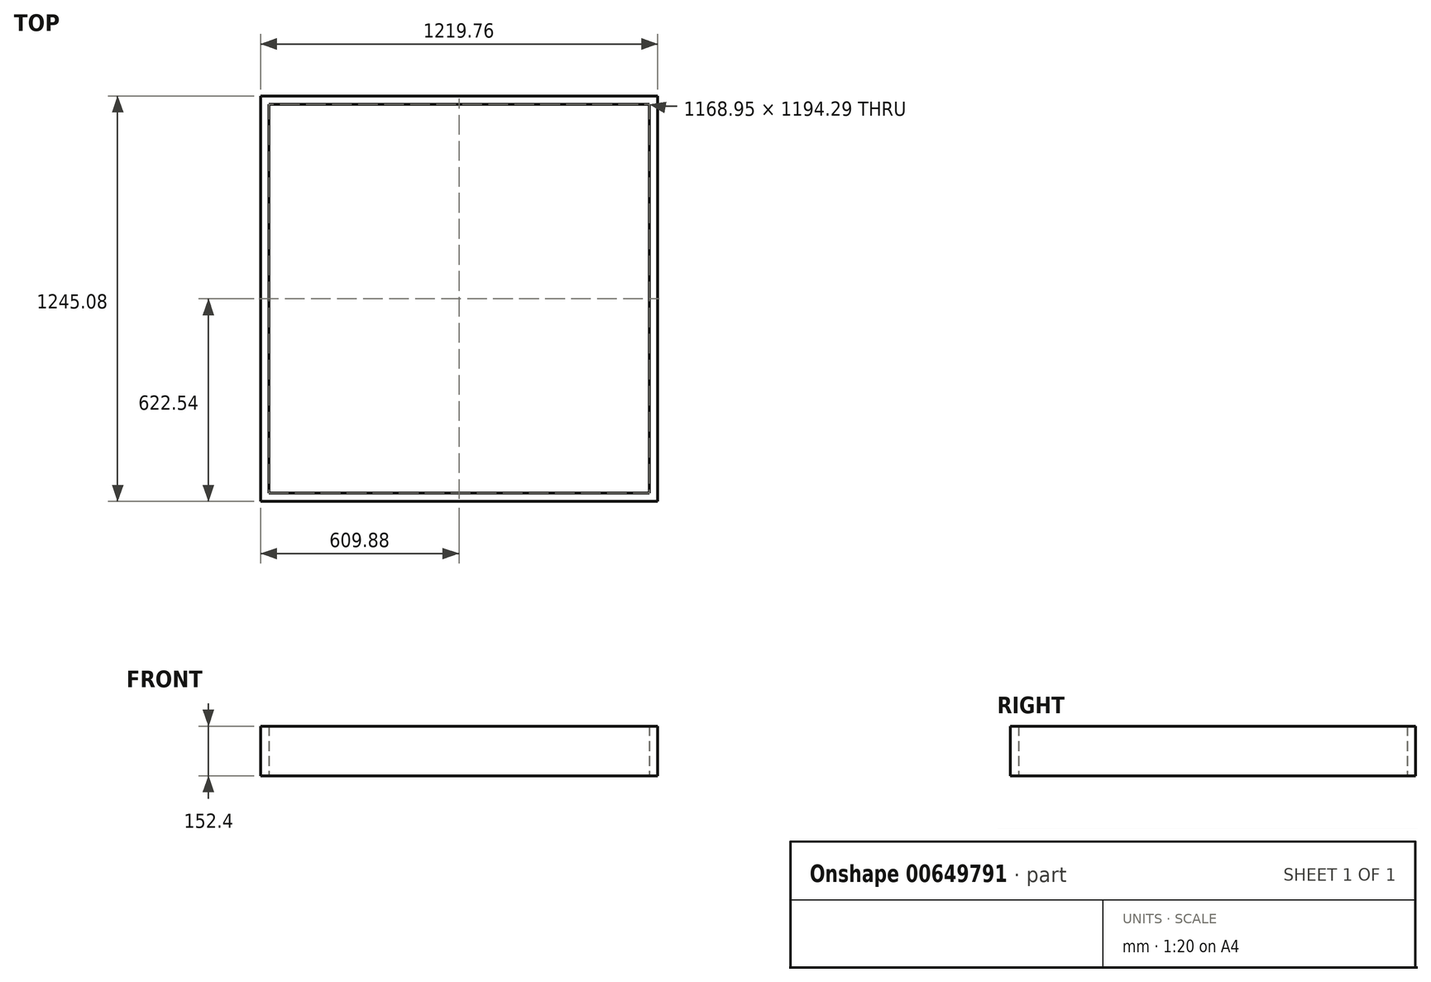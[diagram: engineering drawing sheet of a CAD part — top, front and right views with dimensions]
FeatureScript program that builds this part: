
annotation { "Feature Type Name" : "Feature", "Feature Type Description" : "" }
export const myFeature = defineFeature(function(context is Context, id is Id, definition is map)
    precondition{}
    {
        {
            var Q0;
            Q0=qCreatedBy(makeId("Top.planeOp"),FACE);
            var sketch = newSketch(context, id + "F0", { "sketchPlane" : qUnion([Q0])});
            skLineSegment(sketch, "E0.bottom", {"start": v(584.48, -597.14) * mm, "end": v(-584.48, -597.14) * mm});
            skLineSegment(sketch, "E0.top", {"start": v(584.48, 597.14) * mm, "end": v(-584.48, 597.14) * mm});
            skLineSegment(sketch, "E0.left", {"start": v(584.48, -597.14) * mm, "end": v(584.48, 597.14) * mm});
            skLineSegment(sketch, "E0.right", {"start": v(-584.48, -597.14) * mm, "end": v(-584.48, 597.14) * mm});
            skPoint(sketch, "E0.middle", {"position": v(0, 0) * mm});
            skSolve(sketch);
        }
        {
            var Q0;
            Q0=makeQuery(id+"F0.imprint","IMPRINT",FACE,{"disambiguationData":[TD([[makeQuery(id+"F0.imprint","IMPRINT",EDGE,{"derivedFrom":sQuery(id+"F0.wireOp",EDGE,"E0.bottom")}),-1.0]])]});
            extrude(context, id + "F1", {"entities" : qUnion([Q0]), "depth" : 152.4 * mm, "offsetDistance" : 25.4 * mm});
        }
        {
            var Q0;
            Q0=makeQuery(id+"F1.opExtrude","CAP_FACE",FACE,{"disambiguationData":[OSD([sQuery(id+"F0.wireOp",EDGE,"E0.bottom"),sQuery(id+"F0.wireOp",EDGE,"E0.top"),sQuery(id+"F0.wireOp",EDGE,"E0.left"),sQuery(id+"F0.wireOp",EDGE,"E0.right")])],"isStart":true});
            var Q1;
            Q1=makeQuery(id+"F1.opExtrude","CAP_FACE",FACE,{"disambiguationData":[OSD([sQuery(id+"F0.wireOp",EDGE,"E0.bottom"),sQuery(id+"F0.wireOp",EDGE,"E0.top"),sQuery(id+"F0.wireOp",EDGE,"E0.left"),sQuery(id+"F0.wireOp",EDGE,"E0.right")])],"isStart":false});
            shell(context, id + "F2", {"entities" : qUnion([Q0, Q1]), "thickness" : 25.4 * mm, "oppositeDirection" : true});
        }
    });
